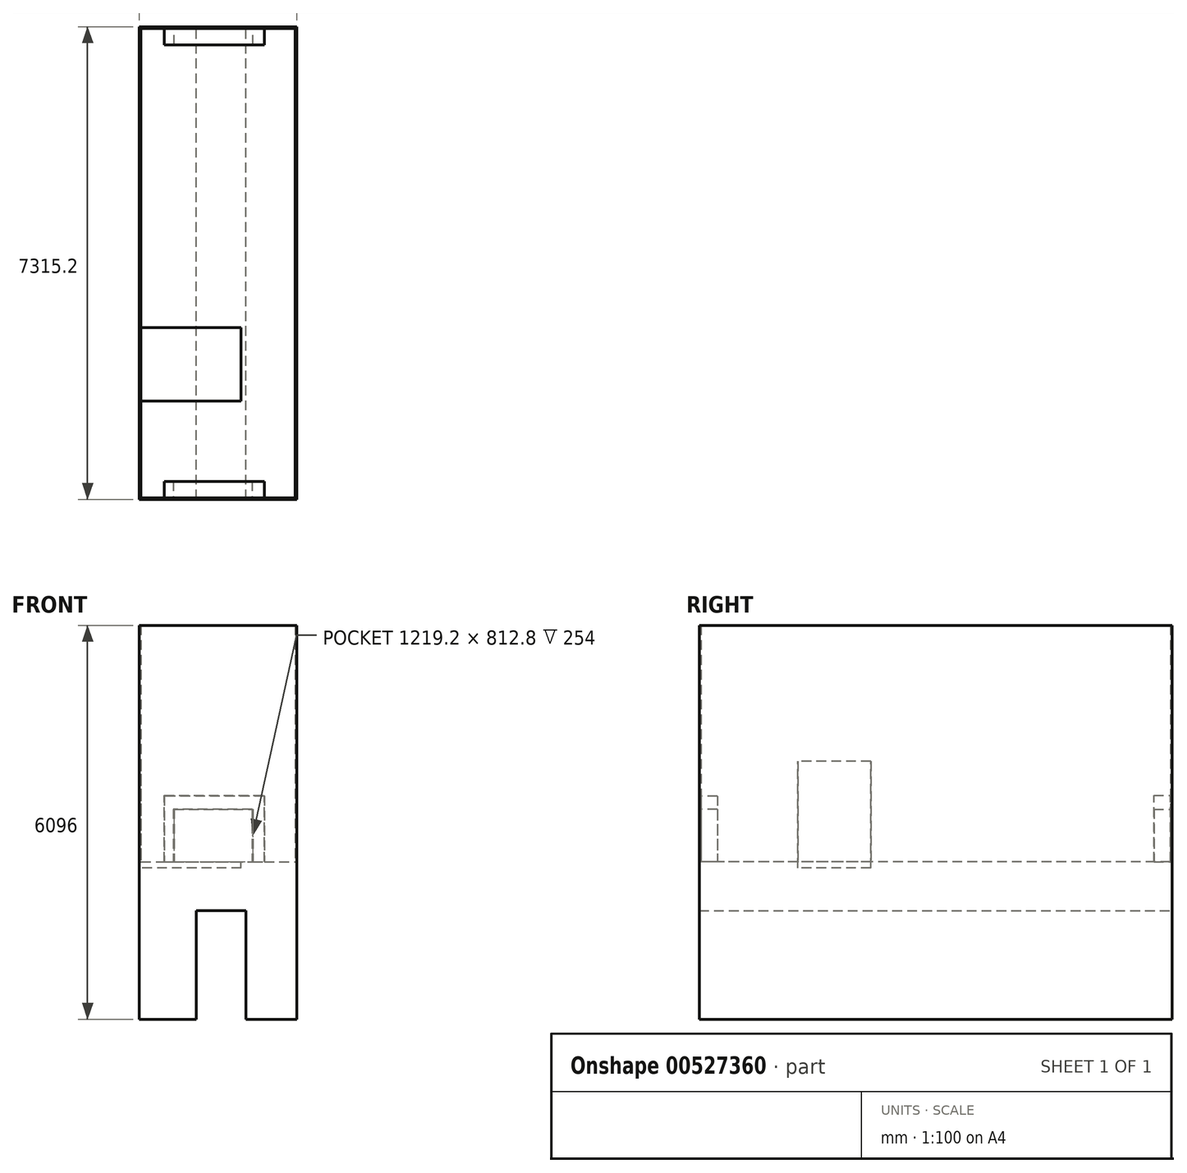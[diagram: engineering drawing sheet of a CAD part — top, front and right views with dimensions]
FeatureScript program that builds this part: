
annotation { "Feature Type Name" : "Feature", "Feature Type Description" : "" }
export const myFeature = defineFeature(function(context is Context, id is Id, definition is map)
    precondition{}
    {
        {
            var Q0;
            Q0=qCreatedBy(makeId("Front.planeOp"),FACE);
            var sketch = newSketch(context, id + "F0", { "sketchPlane" : qUnion([Q0])});
            skLineSegment(sketch, "E0.bottom", {"start": v(-78.27, 2438.4) * mm, "end": v(2360.13, 2438.4) * mm});
            skLineSegment(sketch, "E0.top", {"start": v(-78.27, 0) * mm, "end": v(2360.13, 0) * mm});
            skLineSegment(sketch, "E0.left", {"start": v(-78.27, 2438.4) * mm, "end": v(-78.27, 0) * mm});
            skLineSegment(sketch, "E0.right", {"start": v(2360.13, 2438.4) * mm, "end": v(2360.13, 0) * mm});
            skLineSegment(sketch, "E1.bottom", {"start": v(1571.3, 0) * mm, "end": v(802.6, 0) * mm});
            skLineSegment(sketch, "E1.top", {"start": v(1571.3, 1679.43) * mm, "end": v(802.6, 1679.43) * mm});
            skLineSegment(sketch, "E1.left", {"start": v(1571.3, 0) * mm, "end": v(1571.3, 1679.43) * mm});
            skLineSegment(sketch, "E1.right", {"start": v(802.6, 0) * mm, "end": v(802.6, 1679.43) * mm});
            skSolve(sketch);
        }
        {
            var Q0;
            Q0=makeQuery(id+"F0.imprint","IMPRINT",FACE,{"disambiguationData":[TD([[makeQuery(id+"F0.imprint","IMPRINT",EDGE,{"derivedFrom":sQuery(id+"F0.wireOp",EDGE,"E0.bottom")}),-1.0]])]});
            extrude(context, id + "F1", {"entities" : qUnion([Q0]), "depth" : 7315.2 * mm, "offsetDistance" : 25.4 * mm});
        }
        {
            var Q0;
            Q0=makeQuery(id+"F1.opExtrude","SWEPT_FACE",FACE,{"disambiguationData":[OSD([sQuery(id+"F0.wireOp",EDGE,"E0.bottom")])]});
            var sketch = newSketch(context, id + "F2", { "sketchPlane" : qUnion([Q0])});
            skLineSegment(sketch, "E2.bottom", {"start": v(-78.27, -7315.2) * mm, "end": v(2360.13, -7315.2) * mm});
            skLineSegment(sketch, "E2.top", {"start": v(-78.27, -7289.8) * mm, "end": v(2360.13, -7289.8) * mm});
            skLineSegment(sketch, "E2.left", {"start": v(-78.27, -7315.2) * mm, "end": v(-78.27, -7289.8) * mm});
            skLineSegment(sketch, "E2.right", {"start": v(2360.13, -7315.2) * mm, "end": v(2360.13, -7289.8) * mm});
            skLineSegment(sketch, "E3.bottom", {"start": v(-78.27, -7289.8) * mm, "end": v(-52.87, -7289.8) * mm});
            skLineSegment(sketch, "E3.left", {"start": v(-78.27, -7289.8) * mm, "end": v(-78.27, 0) * mm});
            skLineSegment(sketch, "E4.top", {"start": v(-52.87, -25.4) * mm, "end": v(2360.13, -25.4) * mm});
            skLineSegment(sketch, "E4.right", {"start": v(2360.13, 0) * mm, "end": v(2360.13, -25.4) * mm});
            skLineSegment(sketch, "E5.bottom", {"start": v(2360.13, -25.4) * mm, "end": v(2334.73, -25.4) * mm});
            skLineSegment(sketch, "E5.top", {"start": v(2360.13, -7289.8) * mm, "end": v(2334.73, -7289.8) * mm});
            skLineSegment(sketch, "E5.left", {"start": v(2360.13, -25.4) * mm, "end": v(2360.13, -7289.8) * mm});
            skLineSegment(sketch, "E5.right", {"start": v(2334.73, -25.4) * mm, "end": v(2334.73, -7289.8) * mm});
            skLineSegment(sketch, "E6", {"start": v(-78.27, 0) * mm, "end": v(-52.87, 0) * mm});
            skLineSegment(sketch, "E7", {"start": v(-52.87, 0) * mm, "end": v(-52.87, -25.4) * mm});
            skLineSegment(sketch, "E8", {"start": v(-52.87, -25.4) * mm, "end": v(-52.87, -7289.8) * mm});
            skLineSegment(sketch, "E9", {"start": v(-52.87, 0) * mm, "end": v(2360.13, 0) * mm});
            skSolve(sketch);
        }
        {
            var Q0;
            Q0 = qSketchRegion(id + "F2", true);
            extrude(context, id + "F3", {"entities" : qUnion([Q0]), "operationType" : NewBodyOperationType.ADD, "depth" : 3657.6 * mm, "offsetDistance" : 25.4 * mm});
        }
        {
            var Q0;
            Q0=makeQuery(id+"F3.boolean.opBoolean","MERGE",FACE,{"derivedFrom":[makeQuery(id+"F1.opExtrude","SWEPT_FACE",FACE,{"disambiguationData":[OSD([sQuery(id+"F0.wireOp",EDGE,"E0.left")])]}),makeQuery(id+"F3.opExtrude","SWEPT_FACE",FACE,{"disambiguationData":[OSD([sQuery(id+"F2.wireOp",EDGE,"E2.left"),sQuery(id+"F2.wireOp",EDGE,"E3.left")])]})]});
            var sketch = newSketch(context, id + "F4", { "sketchPlane" : qUnion([Q0])});
            skLineSegment(sketch, "E10.bottom", {"start": v(4660.23, 2340.27) * mm, "end": v(5791.2, 2340.27) * mm});
            skLineSegment(sketch, "E10.top", {"start": v(4660.23, 3988.6) * mm, "end": v(5791.2, 3988.6) * mm});
            skLineSegment(sketch, "E10.left", {"start": v(4660.23, 2340.27) * mm, "end": v(4660.23, 3988.6) * mm});
            skLineSegment(sketch, "E10.right", {"start": v(5791.2, 2340.27) * mm, "end": v(5791.2, 3988.6) * mm});
            skSolve(sketch);
        }
        {
            var Q0;
            Q0=makeQuery(id+"F4.imprint","IMPRINT",FACE,{"disambiguationData":[TD([[makeQuery(id+"F4.imprint","IMPRINT",EDGE,{"derivedFrom":sQuery(id+"F4.wireOp",EDGE,"E10.bottom")}),1.0]])]});
            extrude(context, id + "F5", {"entities" : qUnion([Q0]), "operationType" : NewBodyOperationType.REMOVE, "oppositeDirection" : true, "depth" : 1574.8 * mm, "offsetDistance" : 25.4 * mm});
        }
        {
            var Q0;
            Q0=makeQuery(id+"F3.opExtrude","SWEPT_FACE",FACE,{"disambiguationData":[OSD([sQuery(id+"F2.wireOp",EDGE,"E4.top")])]});
            var sketch = newSketch(context, id + "F6", { "sketchPlane" : qUnion([Q0])});
            skLineSegment(sketch, "E11.bottom", {"start": v(458.73, 3251.2) * mm, "end": v(1677.93, 3251.2) * mm});
            skLineSegment(sketch, "E11.top", {"start": v(458.73, 2438.4) * mm, "end": v(1677.93, 2438.4) * mm});
            skLineSegment(sketch, "E11.left", {"start": v(458.73, 3251.2) * mm, "end": v(458.73, 2438.4) * mm});
            skLineSegment(sketch, "E11.right", {"start": v(1677.93, 3251.2) * mm, "end": v(1677.93, 2438.4) * mm});
            skLineSegment(sketch, "E12.bottom", {"start": v(306.1, 2438.4) * mm, "end": v(1858.34, 2438.4) * mm});
            skLineSegment(sketch, "E12.top", {"start": v(306.1, 3463.63) * mm, "end": v(1858.34, 3463.63) * mm});
            skLineSegment(sketch, "E12.left", {"start": v(306.1, 2438.4) * mm, "end": v(306.1, 3463.63) * mm});
            skLineSegment(sketch, "E12.right", {"start": v(1858.34, 2438.4) * mm, "end": v(1858.34, 3463.63) * mm});
            skSolve(sketch);
        }
        {
            var Q0;
            Q0=makeQuery(id+"F6.imprint","IMPRINT",FACE,{"disambiguationData":[TD([[makeQuery(id+"F6.imprint","IMPRINT",EDGE,{"derivedFrom":sQuery(id+"F6.wireOp",EDGE,"E11.bottom")}),1.0]])]});
            extrude(context, id + "F7", {"entities" : qUnion([Q0]), "operationType" : NewBodyOperationType.ADD, "depth" : 254 * mm, "offsetDistance" : 25.4 * mm});
        }
        {
            var Q0;
            Q0=makeQuery(id+"F3.opExtrude","SWEPT_FACE",FACE,{"disambiguationData":[OSD([sQuery(id+"F2.wireOp",EDGE,"E2.top")])]});
            var sketch = newSketch(context, id + "F8", { "sketchPlane" : qUnion([Q0])});
            skLineSegment(sketch, "E13.bottom", {"start": v(-1664.3, 3251.2) * mm, "end": v(-445.1, 3251.2) * mm});
            skLineSegment(sketch, "E13.top", {"start": v(-1664.3, 2438.4) * mm, "end": v(-445.1, 2438.4) * mm});
            skLineSegment(sketch, "E13.left", {"start": v(-1664.3, 3251.2) * mm, "end": v(-1664.3, 2438.4) * mm});
            skLineSegment(sketch, "E13.right", {"start": v(-445.1, 3251.2) * mm, "end": v(-445.1, 2438.4) * mm});
            skLineSegment(sketch, "E14.bottom", {"start": v(-1856.81, 3454.4) * mm, "end": v(-304.74, 3454.4) * mm});
            skLineSegment(sketch, "E14.top", {"start": v(-1856.81, 2438.4) * mm, "end": v(-304.74, 2438.4) * mm});
            skLineSegment(sketch, "E14.left", {"start": v(-1856.81, 3454.4) * mm, "end": v(-1856.81, 2438.4) * mm});
            skLineSegment(sketch, "E14.right", {"start": v(-304.74, 3454.4) * mm, "end": v(-304.74, 2438.4) * mm});
            skSolve(sketch);
        }
        {
            var Q0;
            Q0=makeQuery(id+"F8.imprint","IMPRINT",FACE,{"disambiguationData":[TD([[makeQuery(id+"F8.imprint","IMPRINT",EDGE,{"derivedFrom":sQuery(id+"F8.wireOp",EDGE,"E13.bottom")}),1.0]])]});
            extrude(context, id + "F9", {"entities" : qUnion([Q0]), "operationType" : NewBodyOperationType.ADD, "depth" : 254 * mm, "offsetDistance" : 25.4 * mm});
        }
    });
